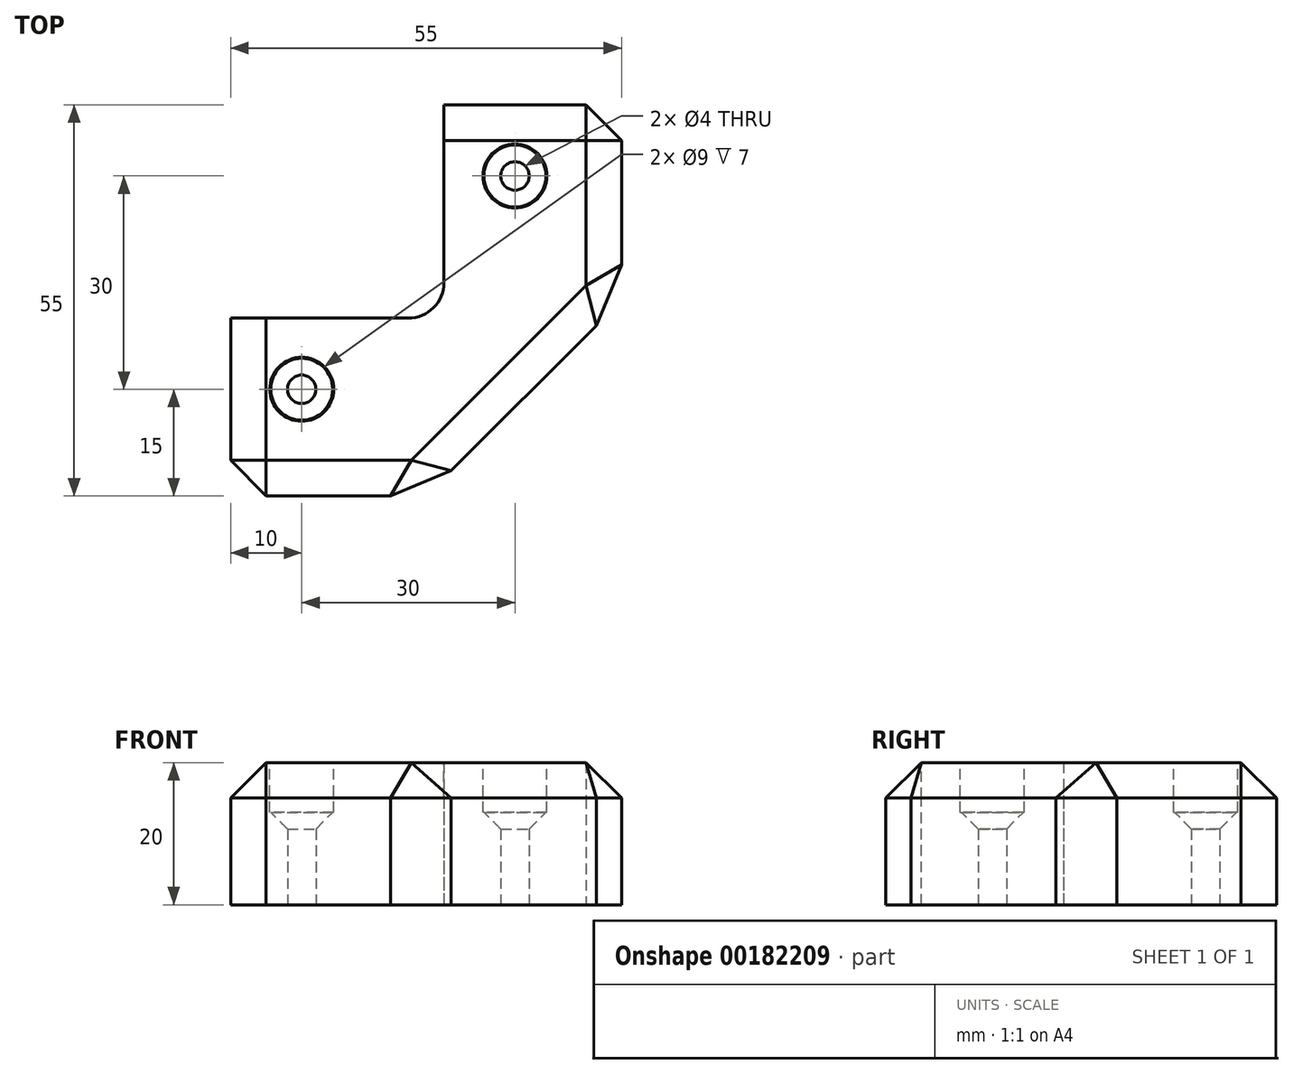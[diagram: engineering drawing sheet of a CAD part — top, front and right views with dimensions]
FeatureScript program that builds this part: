
annotation { "Feature Type Name" : "Feature", "Feature Type Description" : "" }
export const myFeature = defineFeature(function(context is Context, id is Id, definition is map)
    precondition{}
    {
        {
            var Q0;
            Q0=qCreatedBy(makeId("Top.planeOp"),FACE);
            var sketch = newSketch(context, id + "F0", { "sketchPlane" : qUnion([Q0])});
            skLineSegment(sketch, "E0", {"start": v(0, 55) * mm, "end": v(0, 0) * mm});
            skLineSegment(sketch, "E1", {"start": v(0, 0) * mm, "end": v(-55, 0) * mm});
            skLineSegment(sketch, "E2", {"start": v(-55, 0) * mm, "end": v(-55, 25) * mm});
            skLineSegment(sketch, "E3", {"start": v(-55, 25) * mm, "end": v(-25, 25) * mm});
            skLineSegment(sketch, "E4", {"start": v(-25, 25) * mm, "end": v(-25, 55) * mm});
            skLineSegment(sketch, "E5", {"start": v(-25, 55) * mm, "end": v(0, 55) * mm});
            skLineSegment(sketch, "E6", {"start": v(-27.5, 0) * mm, "end": v(0, 27.5) * mm});
            skSolve(sketch);
        }
        {
            var Q0;
            {var subQ0=sQuery(id+"F0.wireOp",EDGE,"E2");Q0=makeQuery(id+"F0.imprint","IMPRINT",FACE,{"disambiguationData":[TD([[makeQuery(id+"F0.imprint","IMPRINT",EDGE,{"derivedFrom":subQ0}),-1.0]])]});}
            extrude(context, id + "F1", {"entities" : qUnion([Q0]), "depth" : 20 * mm});
        }
        {
            var Q0;
            Q0=makeQuery(id+"F1.opExtrude","SWEPT_EDGE",EDGE,{"disambiguationData":[OSD([sQuery(id+"F0.wireOp",EDGE,"E0"),sQuery(id+"F0.wireOp",EDGE,"E1")])]});
            var Q1;
            Q1=makeQuery(id+"F1.opExtrude","CAP_EDGE",EDGE,{"disambiguationData":[OSD([sQuery(id+"F0.wireOp",EDGE,"E1")])],"isStart":false});
            var Q2;
            Q2=makeQuery(id+"F1.opExtrude","CAP_EDGE",EDGE,{"disambiguationData":[OSD([sQuery(id+"F0.wireOp",EDGE,"E0")])],"isStart":false});
            var Q3;
            Q3=makeQuery(id+"F1.opExtrude","CAP_EDGE",EDGE,{"disambiguationData":[OSD([sQuery(id+"F0.wireOp",EDGE,"E2")])],"isStart":false});
            var Q4;
            Q4=makeQuery(id+"F1.opExtrude","SWEPT_EDGE",EDGE,{"disambiguationData":[OSD([sQuery(id+"F0.wireOp",EDGE,"E1"),sQuery(id+"F0.wireOp",EDGE,"E2")])]});
            var Q5;
            Q5=makeQuery(id+"F1.opExtrude","CAP_EDGE",EDGE,{"disambiguationData":[OSD([sQuery(id+"F0.wireOp",EDGE,"E5")])],"isStart":false});
            var Q6;
            Q6=makeQuery(id+"F1.opExtrude","SWEPT_EDGE",EDGE,{"disambiguationData":[OSD([sQuery(id+"F0.wireOp",EDGE,"E0"),sQuery(id+"F0.wireOp",EDGE,"E5")])]});
            var Q7;
            Q7=makeQuery(id+"F1.opExtrude","CAP_EDGE",EDGE,{"disambiguationData":[OSD([sQuery(id+"F0.wireOp",EDGE,"E6")])],"isStart":false});
            chamfer(context, id + "F2", {"entities" : qUnion([Q0, Q1, Q2, Q3, Q4, Q5, Q6, Q7]), "width" : 5 * mm, "tangentPropagation" : true});
        }
        {
            var Q0;
            Q0=makeQuery(id+"F1.opExtrude","SWEPT_EDGE",EDGE,{"disambiguationData":[OSD([sQuery(id+"F0.wireOp",EDGE,"E3"),sQuery(id+"F0.wireOp",EDGE,"E4")])]});
            fillet(context, id + "F3", {"entities" : qUnion([Q0]), "radius" : 5 * mm, "tangentPropagation" : true, "allowEdgeOverflow" : false});
        }
        {
            var Q0;
            Q0=makeQuery(id+"F1.opExtrude","CAP_FACE",FACE,{"disambiguationData":[OSD([sQuery(id+"F0.wireOp",EDGE,"E0"),sQuery(id+"F0.wireOp",EDGE,"E1"),sQuery(id+"F0.wireOp",EDGE,"E2"),sQuery(id+"F0.wireOp",EDGE,"E3"),sQuery(id+"F0.wireOp",EDGE,"E4"),sQuery(id+"F0.wireOp",EDGE,"E5"),sQuery(id+"F0.wireOp",EDGE,"E6")])],"isStart":false});
            cPlane(context, id + "F4", {"entities" : qUnion([Q0]), "cplaneType" : CPlaneType.OFFSET, "offset" : 7 * mm, "oppositeDirection" : true, "width" : 150 * mm, "height" : 150 * mm});
        }
        {
            var Q0;
            Q0=qCreatedBy(id+"F4.planeOp",FACE);
            var sketch = newSketch(context, id + "F5", { "sketchPlane" : qUnion([Q0])});
            skLineSegment(sketch, "E7", {"start": v(0, 0) * mm, "end": v(-45, 0) * mm});
            skLineSegment(sketch, "E8", {"start": v(-45, 0) * mm, "end": v(-45, 15) * mm});
            skLineSegment(sketch, "E9", {"start": v(-45, 15) * mm, "end": v(-15, 15) * mm});
            skLineSegment(sketch, "E10", {"start": v(-15, 15) * mm, "end": v(-15, 45) * mm});
            skSolve(sketch);
        }
        {
            var Q0;
            Q0=sQuery(id+"F5.wireOp",VERTEX,"E9.start");
            var Q1;
            Q1=sQuery(id+"F5.wireOp",VERTEX,"E10.end");
            var Q2;
            Q2=makeQuery(id+"F1.opExtrude","SWEPT_BODY",BODY,{"disambiguationData":[OSD([sQuery(id+"F0.wireOp",EDGE,"E0"),sQuery(id+"F0.wireOp",EDGE,"E1"),sQuery(id+"F0.wireOp",EDGE,"E2"),sQuery(id+"F0.wireOp",EDGE,"E3"),sQuery(id+"F0.wireOp",EDGE,"E4"),sQuery(id+"F0.wireOp",EDGE,"E5"),sQuery(id+"F0.wireOp",EDGE,"E6")])]});
            hole(context, id + "F6", {"style" : HoleStyle.C_SINK, "endStyle" : HoleEndStyle.THROUGH, "holeDiameter" : 4 * mm, "cSinkDiameter" : 8.7 * mm, "cSinkAngle" : 90 * degree, "locations" : qUnion([Q0, Q1]), "scope" : qUnion([Q2]), "isTappedThrough" : true, "startStyle" : HoleStartStyle.PART});
        }
        {
            var Q0;
            Q0=makeQuery(id+"F1.opExtrude","CAP_FACE",FACE,{"disambiguationData":[OSD([sQuery(id+"F0.wireOp",EDGE,"E0"),sQuery(id+"F0.wireOp",EDGE,"E1"),sQuery(id+"F0.wireOp",EDGE,"E2"),sQuery(id+"F0.wireOp",EDGE,"E3"),sQuery(id+"F0.wireOp",EDGE,"E4"),sQuery(id+"F0.wireOp",EDGE,"E5"),sQuery(id+"F0.wireOp",EDGE,"E6")])],"isStart":false});
            var sketch = newSketch(context, id + "F7", { "sketchPlane" : qUnion([Q0])});
            skLineSegment(sketch, "E11", {"start": v(-60, 15) * mm, "end": v(-45, 15) * mm});
            skLineSegment(sketch, "E12", {"start": v(-45, 15) * mm, "end": v(-15, 15) * mm});
            skLineSegment(sketch, "E13", {"start": v(-15, 15) * mm, "end": v(-15, 45) * mm});
            skPoint(sketch, "E13.endSnap0", {"position": v(0, 45) * mm});
            skCircle(sketch, "E14", {"center": v(-45, 15) * mm, "radius": 4.5 * mm});
            skCircle(sketch, "E15", {"center": v(-15, 45) * mm, "radius": 4.5 * mm});
            skSolve(sketch);
        }
        {
            var Q0;
            Q0 = qSketchRegion(id + "F7", true);
            var Q1;
            {var subQ0=sQuery(id+"F7.wireOp",EDGE,"E12");var subQ1=sQuery(id+"F7.wireOp",EDGE,"E11");var subQ2=makeQuery(id+"F7.imprint","INTERSECT",VERTEX,{"derivedFrom":[subQ1,subQ0]});Q1=makeQuery(id+"F7.imprint","IMPRINT",FACE,{"disambiguationData":[TD([[makeQuery(id+"F7.imprint","IMPRINT",EDGE,{"disambiguationData":[TD([[subQ2,1.0]])],"derivedFrom":subQ1}),1.0]])]});}
            extrude(context, id + "F8", {"entities" : qUnion([Q0, Q1]), "operationType" : NewBodyOperationType.REMOVE, "oppositeDirection" : true, "depth" : 7 * mm});
        }
    });
